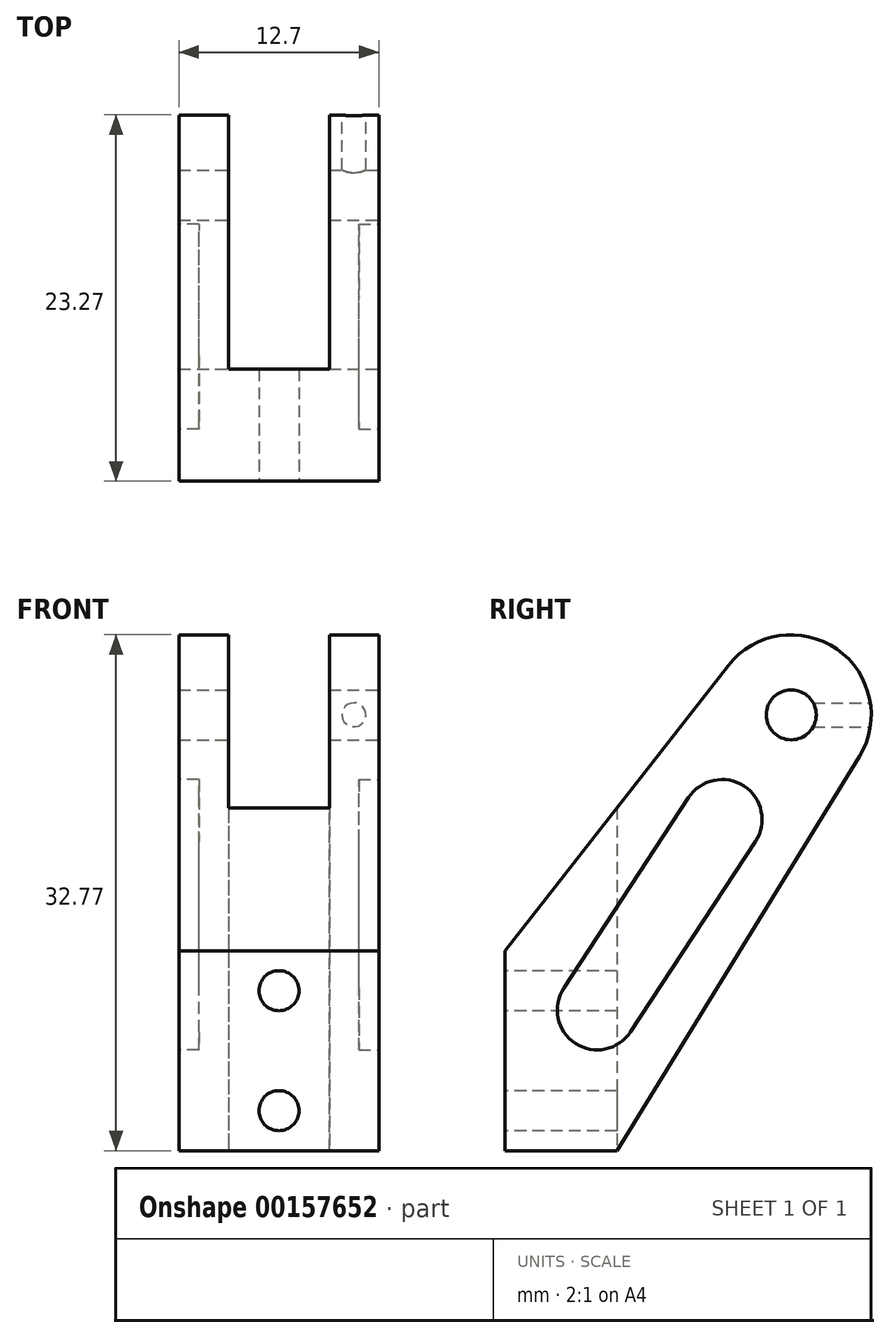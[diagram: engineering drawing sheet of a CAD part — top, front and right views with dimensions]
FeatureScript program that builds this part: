
annotation { "Feature Type Name" : "Feature", "Feature Type Description" : "" }
export const myFeature = defineFeature(function(context is Context, id is Id, definition is map)
    precondition{}
    {
        {
            var Q0;
            Q0=qCreatedBy(makeId("Right.planeOp"),FACE);
            var sketch = newSketch(context, id + "F0", { "sketchPlane" : qUnion([Q0])});
            skCircle(sketch, "E0", {"center": v(18.19, 27.69) * mm, "radius": 1.59 * mm});
            skArc(sketch, "E1", {"start": v(22.51, 25.02) * mm, "mid": v(21.09, 31.86) * mm, "end": v(14.19, 30.82) * mm, "construction": true});
            skLineSegment(sketch, "E2", {"start": v(0, 12.7) * mm, "end": v(14.19, 30.82) * mm});
            skLineSegment(sketch, "E3", {"start": v(7.11, 0) * mm, "end": v(22.51, 25.02) * mm});
            skArc(sketch, "E4", {"start": v(22.51, 25.02) * mm, "mid": v(21.09, 31.86) * mm, "end": v(14.19, 30.82) * mm});
            skLineSegment(sketch, "E5", {"start": v(0, 12.7) * mm, "end": v(0, 0) * mm});
            skLineSegment(sketch, "E6", {"start": v(0, 0) * mm, "end": v(7.11, 0) * mm});
            skLineSegment(sketch, "E7", {"start": v(19.77, 27.69) * mm, "end": v(23.27, 27.69) * mm});
            skSolve(sketch);
        }
        {
            var Q0;
            Q0=makeQuery(id+"F0.imprint","IMPRINT",FACE,{"disambiguationData":[TD([[makeQuery(id+"F0.imprint","IMPRINT",EDGE,{"derivedFrom":sQuery(id+"F0.wireOp",EDGE,"E0")}),-1.0]])]});
            extrude(context, id + "F1", {"entities" : qUnion([Q0]), "oppositeDirection" : true, "depth" : 12.7 * mm});
        }
        {
            var Q0;
            Q0=makeQuery(id+"F1.opExtrude","SWEPT_FACE",FACE,{"disambiguationData":[OSD([sQuery(id+"F0.wireOp",EDGE,"E5")])]});
            var sketch = newSketch(context, id + "F2", { "sketchPlane" : qUnion([Q0])});
            skCircle(sketch, "E8", {"center": v(-6.35, 2.54) * mm, "radius": 1.27 * mm});
            skPoint(sketch, "E8.centerSnap0", {"position": v(-6.35, 0) * mm});
            skCircle(sketch, "E9", {"center": v(-6.35, 10.16) * mm, "radius": 1.27 * mm});
            skSolve(sketch);
        }
        {
            var Q0;
            Q0=makeQuery(id+"F2.imprint","IMPRINT",FACE,{"disambiguationData":[TD([[makeQuery(id+"F2.imprint","IMPRINT",EDGE,{"derivedFrom":sQuery(id+"F2.wireOp",EDGE,"E9")}),1.0]])]});
            var Q1;
            Q1=makeQuery(id+"F2.imprint","IMPRINT",FACE,{"disambiguationData":[TD([[makeQuery(id+"F2.imprint","IMPRINT",EDGE,{"derivedFrom":sQuery(id+"F2.wireOp",EDGE,"E8")}),1.0]])]});
            extrude(context, id + "F3", {"entities" : qUnion([Q0, Q1]), "operationType" : NewBodyOperationType.REMOVE, "oppositeDirection" : true, "depth" : 25.4 * mm});
        }
        {
            var Q0;
            Q0=makeQuery(id+"F1.opExtrude","SWEPT_FACE",FACE,{"disambiguationData":[OSD([sQuery(id+"F0.wireOp",EDGE,"E6")])]});
            var sketch = newSketch(context, id + "F4", { "sketchPlane" : qUnion([Q0])});
            skLineSegment(sketch, "E10", {"start": v(-6.35, -7.11) * mm, "end": v(-6.35, -21.2) * mm, "construction": true});
            skLineSegment(sketch, "E11.bottom", {"start": v(-7.16, -7.11) * mm, "end": v(-5.54, -7.11) * mm});
            skLineSegment(sketch, "E11.top", {"start": v(-9.55, -27.93) * mm, "end": v(-3.15, -27.93) * mm});
            skLineSegment(sketch, "E11.left", {"start": v(-9.55, -9.5) * mm, "end": v(-9.55, -27.93) * mm});
            skLineSegment(sketch, "E11.right", {"start": v(-3.15, -9.5) * mm, "end": v(-3.15, -27.93) * mm});
            skPoint(sketch, "E11.middle", {"position": v(-6.35, -17.52) * mm});
            skPoint(sketch, "E12.visualSharp", {"position": v(-3.15, -7.11) * mm});
            skPoint(sketch, "E13.visualSharp", {"position": v(-9.55, -7.11) * mm});
            skLineSegment(sketch, "E14", {"start": v(-9.55, -9.5) * mm, "end": v(-9.55, -7.11) * mm});
            skLineSegment(sketch, "E15", {"start": v(-3.15, -9.5) * mm, "end": v(-3.15, -7.11) * mm});
            skSolve(sketch);
        }
        {
            var Q0;
            Q0=makeQuery(id+"F4.imprint","IMPRINT",FACE,{"disambiguationData":[TD([[makeQuery(id+"F4.imprint","IMPRINT",EDGE,{"derivedFrom":sQuery(id+"F4.wireOp",EDGE,"E11.bottom")}),-1.0]])]});
            extrude(context, id + "F5", {"entities" : qUnion([Q0]), "operationType" : NewBodyOperationType.REMOVE, "endBound" : BoundingType.THROUGH_ALL, "oppositeDirection" : true, "depth" : 25.4 * mm});
        }
        {
            var Q0;
            Q0=qCreatedBy(makeId("Front.planeOp"),FACE);
            var Q1;
            Q1=sQuery(id+"F0.wireOp",VERTEX,"E7.end");
            cPlane(context, id + "F6", {"entities" : qUnion([Q0, Q1]), "cplaneType" : CPlaneType.PLANE_POINT, "offset" : 25.4 * mm, "width" : 152.4 * mm, "height" : 152.4 * mm});
        }
        {
            var Q0;
            Q0=qCreatedBy(id+"F6.planeOp",FACE);
            var sketch = newSketch(context, id + "F7", { "sketchPlane" : qUnion([Q0])});
            skLineSegment(sketch, "E16", {"start": v(0, 27.68) * mm, "end": v(-12.84, 27.68) * mm, "construction": true});
            skCircle(sketch, "E17", {"center": v(-1.58, 27.68) * mm, "radius": 0.76 * mm});
            skSolve(sketch);
        }
        {
            var Q0;
            Q0=makeQuery(id+"F7.imprint","IMPRINT",FACE,{"disambiguationData":[TD([[makeQuery(id+"F7.imprint","IMPRINT",EDGE,{"derivedFrom":sQuery(id+"F7.wireOp",EDGE,"E17")}),1.0]])]});
            extrude(context, id + "F8", {"entities" : qUnion([Q0]), "operationType" : NewBodyOperationType.REMOVE, "depth" : 5.08 * mm});
        }
        {
            var Q0;
            Q0=makeQuery(id+"F0.imprint","IMPRINT",FACE,{"disambiguationData":[TD([[makeQuery(id+"F0.imprint","IMPRINT",EDGE,{"derivedFrom":sQuery(id+"F0.wireOp",EDGE,"E0")}),-1.0]])]});
            var sketch = newSketch(context, id + "F9", { "sketchPlane" : qUnion([Q0])});
            skArc(sketch, "E18", {"start": v(3.74, 10.33) * mm, "mid": v(4.47, 6.82) * mm, "end": v(8, 7.55) * mm});
            skArc(sketch, "E19", {"start": v(15.92, 19.64) * mm, "mid": v(15.18, 23.16) * mm, "end": v(11.67, 22.42) * mm});
            skLineSegment(sketch, "E20", {"start": v(3.74, 10.33) * mm, "end": v(11.67, 22.42) * mm});
            skLineSegment(sketch, "E21", {"start": v(8, 7.55) * mm, "end": v(15.92, 19.64) * mm});
            skSolve(sketch);
        }
        {
            var Q0;
            Q0=makeQuery(id+"F9.imprint","IMPRINT",FACE,{"disambiguationData":[TD([[makeQuery(id+"F9.imprint","IMPRINT",EDGE,{"derivedFrom":sQuery(id+"F9.wireOp",EDGE,"E18")}),1.0]])]});
            extrude(context, id + "F10", {"entities" : qUnion([Q0]), "operationType" : NewBodyOperationType.REMOVE, "oppositeDirection" : true, "depth" : 1.27 * mm});
        }
        {
            var Q0;
            Q0=makeQuery(id+"F1.opExtrude","CAP_FACE",FACE,{"disambiguationData":[OSD([sQuery(id+"F0.wireOp",EDGE,"E0"),sQuery(id+"F0.wireOp",EDGE,"E2"),sQuery(id+"F0.wireOp",EDGE,"E3"),sQuery(id+"F0.wireOp",EDGE,"E4"),sQuery(id+"F0.wireOp",EDGE,"E5"),sQuery(id+"F0.wireOp",EDGE,"E6")])],"isStart":false});
            var sketch = newSketch(context, id + "F11", { "sketchPlane" : qUnion([Q0])});
            skLineSegment(sketch, "E22", {"start": v(2.53, 0) * mm, "end": v(2.53, 8.94) * mm, "construction": true});
            skLineSegment(sketch, "E23", {"start": v(4.76, 0) * mm, "end": v(4.76, 21.03) * mm, "construction": true});
            skLineSegment(sketch, "E24", {"start": v(0, -2.75) * mm, "end": v(-5.87, -2.75) * mm, "construction": true});
            skLineSegment(sketch, "E25", {"start": v(0, -6.47) * mm, "end": v(-13.8, -6.47) * mm, "construction": true});
            skArc(sketch, "E26", {"start": v(-8, 7.55) * mm, "mid": v(-4.47, 6.82) * mm, "end": v(-3.74, 10.33) * mm});
            skArc(sketch, "E27", {"start": v(-11.67, 22.42) * mm, "mid": v(-15.18, 23.16) * mm, "end": v(-15.92, 19.64) * mm});
            skLineSegment(sketch, "E28", {"start": v(-8, 7.55) * mm, "end": v(-15.92, 19.64) * mm});
            skLineSegment(sketch, "E29", {"start": v(-3.74, 10.33) * mm, "end": v(-11.67, 22.42) * mm});
            skSolve(sketch);
        }
        {
            var Q0;
            Q0=makeQuery(id+"F11.imprint","IMPRINT",FACE,{"disambiguationData":[TD([[makeQuery(id+"F11.imprint","IMPRINT",EDGE,{"derivedFrom":sQuery(id+"F11.wireOp",EDGE,"E26")}),1.0]])]});
            extrude(context, id + "F12", {"entities" : qUnion([Q0]), "operationType" : NewBodyOperationType.REMOVE, "oppositeDirection" : true, "depth" : 1.27 * mm});
        }
    });
